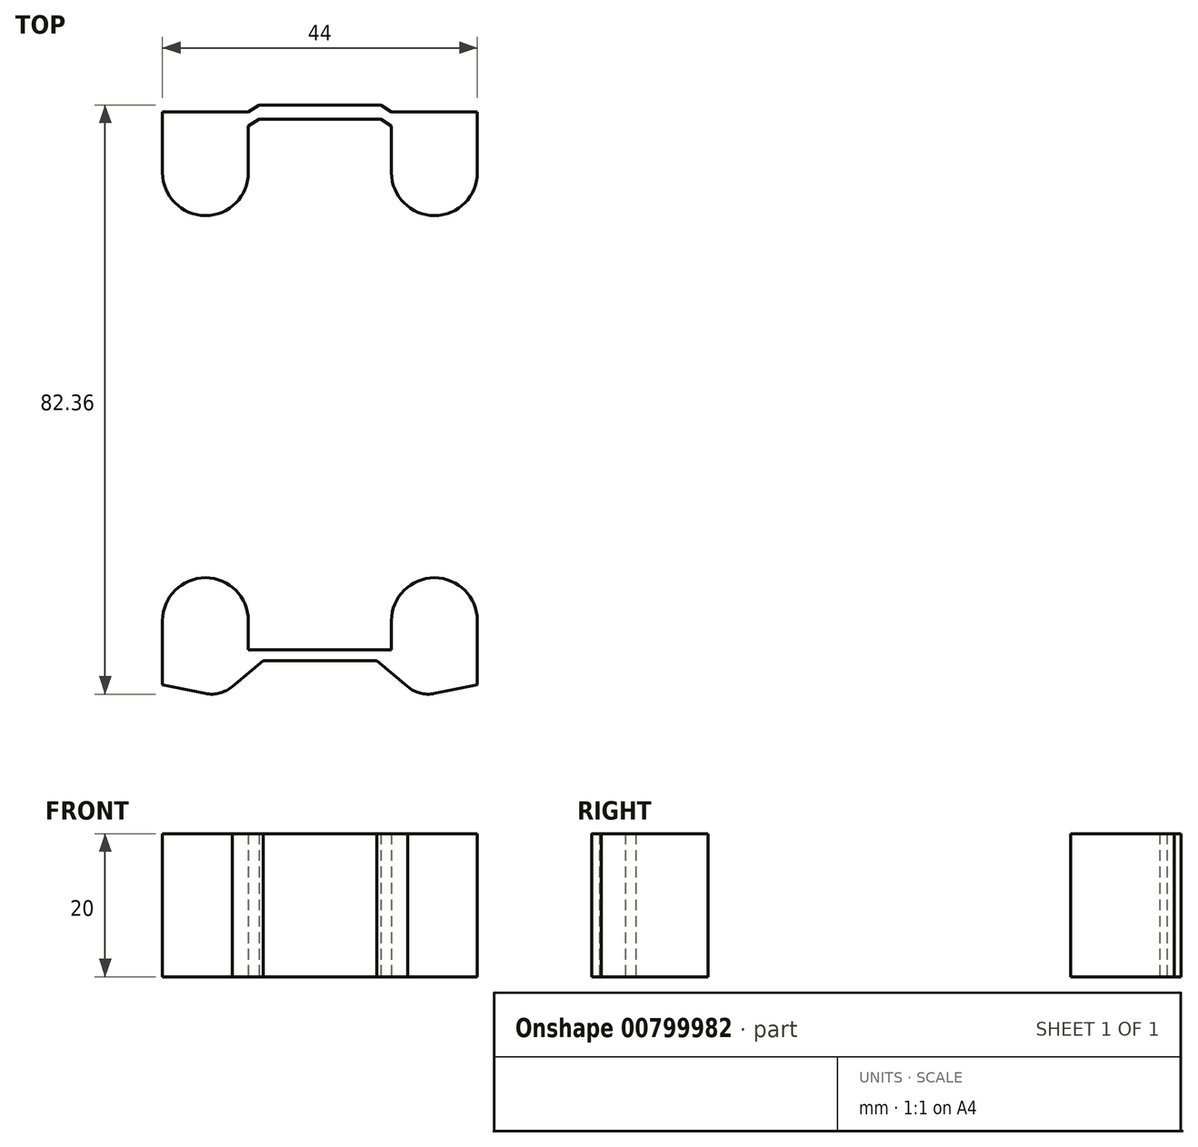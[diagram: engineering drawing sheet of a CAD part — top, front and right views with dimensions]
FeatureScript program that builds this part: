
annotation { "Feature Type Name" : "Feature", "Feature Type Description" : "" }
export const myFeature = defineFeature(function(context is Context, id is Id, definition is map)
    precondition{}
    {
        {
            var Q0;
            Q0=qCreatedBy(makeId("Top.planeOp"),FACE);
            var sketch = newSketch(context, id + "F0", { "sketchPlane" : qUnion([Q0])});
            skLineSegment(sketch, "E0.bottom", {"start": v(-22, 39) * mm, "end": v(22, 39) * mm});
            skLineSegment(sketch, "E0.top", {"start": v(-22, -39) * mm, "end": v(22, -39) * mm});
            skPoint(sketch, "E0.middle", {"position": v(0, 0) * mm});
            skLineSegment(sketch, "E1", {"start": v(-22, 29.23) * mm, "end": v(22, 29.23) * mm, "construction": true});
            skLineSegment(sketch, "E2", {"start": v(-22, -33.4) * mm, "end": v(22, -33.4) * mm, "construction": true});
            skLineSegment(sketch, "E3", {"start": v(16, 39) * mm, "end": v(16, -39) * mm, "construction": true});
            skLineSegment(sketch, "E4", {"start": v(-16, 39) * mm, "end": v(-16, -39) * mm, "construction": true});
            skArc(sketch, "E5", {"start": v(-22, 29.23) * mm, "mid": v(-16, 23.23) * mm, "end": v(-10, 29.23) * mm});
            skLineSegment(sketch, "E6", {"start": v(-10, 29.23) * mm, "end": v(-10, 35.72) * mm});
            skLineSegment(sketch, "E7", {"start": v(-10, 37.72) * mm, "end": v(-22, 37.72) * mm});
            skLineSegment(sketch, "E8", {"start": v(-22, 37.72) * mm, "end": v(-22, 29.23) * mm});
            skArc(sketch, "E9", {"start": v(-10, -33.4) * mm, "mid": v(-16, -27.4) * mm, "end": v(-22, -33.4) * mm});
            skLineSegment(sketch, "E10", {"start": v(-22, -33.4) * mm, "end": v(-22, -42.36) * mm});
            skLineSegment(sketch, "E11", {"start": v(-22, -42.36) * mm, "end": v(-15.98, -43.58) * mm});
            skArc(sketch, "E12", {"start": v(-15.98, -43.58) * mm, "mid": v(-14, -43.53) * mm, "end": v(-12.26, -42.6) * mm});
            skLineSegment(sketch, "E13", {"start": v(0, -39) * mm, "end": v(-7.93, -39) * mm});
            skLineSegment(sketch, "E14", {"start": v(-7.93, -39) * mm, "end": v(-12.26, -42.6) * mm});
            skLineSegment(sketch, "E15", {"start": v(-10, -33.4) * mm, "end": v(-10, -37.5) * mm});
            skLineSegment(sketch, "E16", {"start": v(-10, -37.5) * mm, "end": v(0, -37.5) * mm});
            skLineSegment(sketch, "E17", {"start": v(0, 37.72) * mm, "end": v(0, -39) * mm, "construction": true});
            skLineSegment(sketch, "E18.MirrorCS", {"start": v(10, 37.72) * mm, "end": v(22, 37.72) * mm});
            skLineSegment(sketch, "E19.MirrorCS", {"start": v(10, 29.23) * mm, "end": v(10, 35.72) * mm});
            skArc(sketch, "E20.MirrorCS", {"start": v(22, 29.23) * mm, "mid": v(16, 23.23) * mm, "end": v(10, 29.23) * mm});
            skLineSegment(sketch, "E21.MirrorCS", {"start": v(22, 37.72) * mm, "end": v(22, 29.23) * mm});
            skArc(sketch, "E22.MirrorCS", {"start": v(10, -33.4) * mm, "mid": v(16, -27.4) * mm, "end": v(22, -33.4) * mm});
            skLineSegment(sketch, "E23.MirrorCS", {"start": v(10, -33.4) * mm, "end": v(10, -37.5) * mm});
            skLineSegment(sketch, "E24.MirrorCS", {"start": v(10, -37.5) * mm, "end": v(0, -37.5) * mm});
            skLineSegment(sketch, "E25.MirrorCS", {"start": v(0, -39) * mm, "end": v(7.93, -39) * mm});
            skLineSegment(sketch, "E26.MirrorCS", {"start": v(7.93, -39) * mm, "end": v(12.26, -42.6) * mm});
            skArc(sketch, "E27.MirrorCS", {"start": v(15.98, -43.58) * mm, "mid": v(14, -43.53) * mm, "end": v(12.26, -42.6) * mm});
            skLineSegment(sketch, "E28.MirrorCS", {"start": v(22, -42.36) * mm, "end": v(15.98, -43.58) * mm});
            skLineSegment(sketch, "E29.MirrorCS", {"start": v(22, -33.4) * mm, "end": v(22, -42.36) * mm});
            skLineSegment(sketch, "E30", {"start": v(-10, 37.72) * mm, "end": v(-8.5, 38.7) * mm});
            skLineSegment(sketch, "E31", {"start": v(-8.5, 38.7) * mm, "end": v(0, 38.7) * mm});
            skLineSegment(sketch, "E32.MirrorCS", {"start": v(8.5, 38.7) * mm, "end": v(0, 38.7) * mm});
            skLineSegment(sketch, "E33.MirrorCS", {"start": v(10, 37.72) * mm, "end": v(8.5, 38.7) * mm});
            skLineSegment(sketch, "E34", {"start": v(-8.5, 36.7) * mm, "end": v(8.5, 36.7) * mm});
            skLineSegment(sketch, "E35", {"start": v(-8.5, 36.7) * mm, "end": v(-10, 35.72) * mm});
            skLineSegment(sketch, "E36.MirrorCS", {"start": v(8.5, 36.7) * mm, "end": v(10, 35.72) * mm});
            skPoint(sketch, "E37.orphan", {"position": v(10, 37.72) * mm});
            skLineSegment(sketch, "E38", {"start": v(-14.5, -33.4) * mm, "end": v(-14.5, -20.11) * mm});
            skLineSegment(sketch, "E39", {"start": v(-14.5, -20.11) * mm, "end": v(-16.5, -20.11) * mm});
            skLineSegment(sketch, "E40", {"start": v(-16.5, -20.11) * mm, "end": v(-16.5, -33.4) * mm});
            skSolve(sketch);
        }
        {
            var Q0;
            {var subQ1=sQuery(id+"F0.wireOp",EDGE,"E26.MirrorCS");Q0=makeQuery(id+"F0.imprint","IMPRINT",FACE,{"disambiguationData":[TD([[makeQuery(id+"F0.imprint","IMPRINT",EDGE,{"derivedFrom":subQ1}),1.0]])]});}
            var Q1;
            {var subQ4=sQuery(id+"F0.wireOp",EDGE,"E9");Q1=makeQuery(id+"F0.imprint","IMPRINT",FACE,{"disambiguationData":[TD([[makeQuery(id+"F0.imprint","IMPRINT",EDGE,{"derivedFrom":subQ4}),1.0]])]});}
            var Q2;
            {var subQ4=sQuery(id+"F0.wireOp",EDGE,"E11");Q2=makeQuery(id+"F0.imprint","IMPRINT",FACE,{"disambiguationData":[TD([[makeQuery(id+"F0.imprint","IMPRINT",EDGE,{"derivedFrom":subQ4}),1.0]])]});}
            var Q3;
            Q3=makeQuery(id+"F0.imprint","IMPRINT",FACE,{"disambiguationData":[TD([[makeQuery(id+"F0.imprint","IMPRINT",EDGE,{"derivedFrom":sQuery(id+"F0.wireOp",EDGE,"E5")}),1.0]])]});
            var Q4;
            Q4=makeQuery(id+"F0.imprint","IMPRINT",FACE,{"disambiguationData":[TD([[makeQuery(id+"F0.imprint","IMPRINT",EDGE,{"derivedFrom":sQuery(id+"F0.wireOp",EDGE,"E18.MirrorCS")}),-1.0]])]});
            extrude(context, id + "F1", {"entities" : qUnion([Q0, Q1, Q2, Q3, Q4]), "depth" : 20 * mm, "offsetDistance" : 25 * mm});
        }
    });
